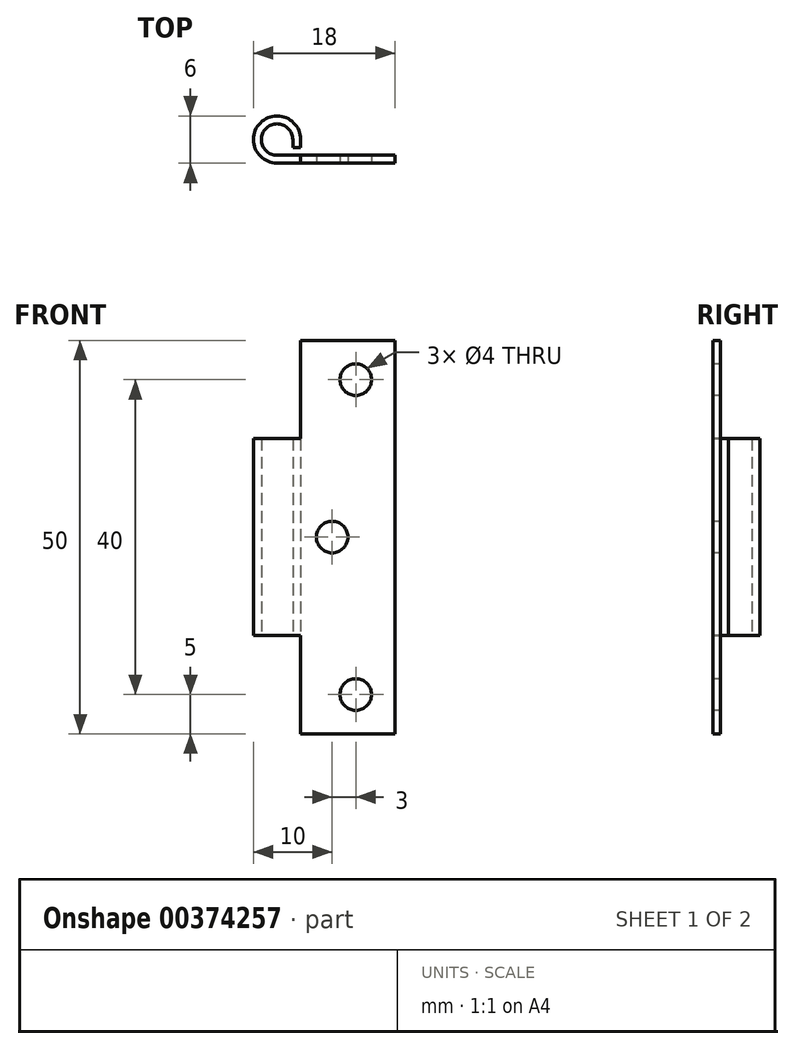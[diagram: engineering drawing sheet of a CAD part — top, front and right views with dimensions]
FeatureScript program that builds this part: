
annotation { "Feature Type Name" : "Feature", "Feature Type Description" : "" }
export const myFeature = defineFeature(function(context is Context, id is Id, definition is map)
    precondition{}
    {
        {
            var Q0;
            Q0=qCreatedBy(makeId("Top.planeOp"),FACE);
            var sketch = newSketch(context, id + "F0", { "sketchPlane" : qUnion([Q0])});
            skLineSegment(sketch, "E0", {"start": v(0, 1) * mm, "end": v(15, 1) * mm});
            skLineSegment(sketch, "E1", {"start": v(15, 1) * mm, "end": v(15, 0) * mm});
            skLineSegment(sketch, "E2", {"start": v(15, 0) * mm, "end": v(0, 0) * mm});
            skArc(sketch, "E3", {"start": v(2, 3) * mm, "mid": v(-1.41, 4.41) * mm, "end": v(0, 1) * mm});
            skLineSegment(sketch, "E4", {"start": v(2, 3) * mm, "end": v(2, 2) * mm});
            skLineSegment(sketch, "E5", {"start": v(2, 2) * mm, "end": v(3, 2) * mm});
            skLineSegment(sketch, "E6", {"start": v(3, 2) * mm, "end": v(3, 3) * mm});
            skArc(sketch, "E7", {"start": v(3, 3) * mm, "mid": v(-2.12, 5.12) * mm, "end": v(0, 0) * mm});
            skSolve(sketch);
        }
        {
            var Q0;
            Q0=makeQuery(id+"F0.imprint","IMPRINT",FACE,{"disambiguationData":[TD([[makeQuery(id+"F0.imprint","IMPRINT",EDGE,{"derivedFrom":sQuery(id+"F0.wireOp",EDGE,"E0")}),-1.0]])]});
            extrude(context, id + "F1", {"entities" : qUnion([Q0]), "depth" : 50 * mm});
        }
        {
            var Q0;
            Q0=qCreatedBy(makeId("Front.planeOp"),FACE);
            var sketch = newSketch(context, id + "F2", { "sketchPlane" : qUnion([Q0])});
            skPoint(sketch, "E8", {"position": v(10, 45) * mm});
            skPoint(sketch, "E9", {"position": v(7, 25) * mm});
            skPoint(sketch, "E10", {"position": v(10, 5) * mm});
            skLineSegment(sketch, "E11.bottom", {"start": v(-5, 50) * mm, "end": v(3, 50) * mm});
            skLineSegment(sketch, "E11.top", {"start": v(-5, 37.5) * mm, "end": v(3, 37.5) * mm});
            skLineSegment(sketch, "E11.left", {"start": v(-5, 50) * mm, "end": v(-5, 37.5) * mm});
            skLineSegment(sketch, "E11.right", {"start": v(3, 50) * mm, "end": v(3, 37.5) * mm});
            skLineSegment(sketch, "E12.bottom", {"start": v(-5, 0) * mm, "end": v(3, 0) * mm});
            skLineSegment(sketch, "E12.top", {"start": v(-5, 12.5) * mm, "end": v(3, 12.5) * mm});
            skLineSegment(sketch, "E12.left", {"start": v(-5, 0) * mm, "end": v(-5, 12.5) * mm});
            skLineSegment(sketch, "E12.right", {"start": v(3, 0) * mm, "end": v(3, 12.5) * mm});
            skSolve(sketch);
        }
        {
            var Q0;
            Q0=sQuery(id+"F2.wireOp",VERTEX,"E8");
            var Q1;
            Q1=sQuery(id+"F2.wireOp",VERTEX,"E9");
            var Q2;
            Q2=sQuery(id+"F2.wireOp",VERTEX,"E10");
            var Q3;
            Q3=makeQuery(id+"F1.opExtrude","SWEPT_BODY",BODY,{"disambiguationData":[OSD([sQuery(id+"F0.wireOp",EDGE,"E0"),sQuery(id+"F0.wireOp",EDGE,"E1"),sQuery(id+"F0.wireOp",EDGE,"E2"),sQuery(id+"F0.wireOp",EDGE,"E3"),sQuery(id+"F0.wireOp",EDGE,"E4"),sQuery(id+"F0.wireOp",EDGE,"E5"),sQuery(id+"F0.wireOp",EDGE,"E6"),sQuery(id+"F0.wireOp",EDGE,"E7")])]});
            hole(context, id + "F3", {"style" : HoleStyle.SIMPLE, "endStyle" : HoleEndStyle.BLIND, "holeDiameter" : 4 * mm, "holeDepth" : 10 * mm, "isTappedThrough" : true, "tappedDepth" : 12 * mm, "tapClearance" : 3, "locations" : qUnion([Q0, Q1, Q2]), "scope" : qUnion([Q3])});
        }
        {
            var Q0;
            Q0=makeQuery(id+"F2.imprint","IMPRINT",FACE,{"disambiguationData":[TD([[makeQuery(id+"F2.imprint","IMPRINT",EDGE,{"derivedFrom":sQuery(id+"F2.wireOp",EDGE,"E11.bottom")}),-1.0]])]});
            var Q1;
            Q1=makeQuery(id+"F2.imprint","IMPRINT",FACE,{"disambiguationData":[TD([[makeQuery(id+"F2.imprint","IMPRINT",EDGE,{"derivedFrom":sQuery(id+"F2.wireOp",EDGE,"E12.bottom")}),1.0]])]});
            extrude(context, id + "F4", {"entities" : qUnion([Q0, Q1]), "operationType" : NewBodyOperationType.REMOVE, "oppositeDirection" : true, "depth" : 25 * mm});
        }
    });
